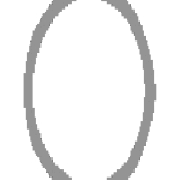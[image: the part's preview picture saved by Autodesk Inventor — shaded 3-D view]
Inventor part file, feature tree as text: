
AUTODESK INVENTOR PART (.ipt)
format: ipt  version: 2021 (Build 250183000, 183)  size: 111,616 bytes
history: native  units: in
note: dims shown in document units (in); Inventor stores cm internally (conversion verified against a paired STEP export)
features: other x4, sketch x3, plane x1
ambient origin geometry x8: Origin, YZ Plane, XZ Plane, XY Plane, X Axis, Y Axis, Z Axis, Center Point
bodies: Solid1 (feature_tree), Body (feature_tree)
feature tree (8):
  other  "Driven Length"
  other  "Frame Generator"
  other  "Start Plane"
  other  "End Plane"
  sketch  "Sketch"  dims[d2=6.7082in d4=-0.0in d5=6.7082in d6=0.12in d7=0.0in d8=90.0deg d9=6.7082in]
  sketch  "Sketch2"  dims[d0=1.0in]
  plane  "Work Plane3"
  sketch  "Sketch3"  dims[d1=0.065in]
